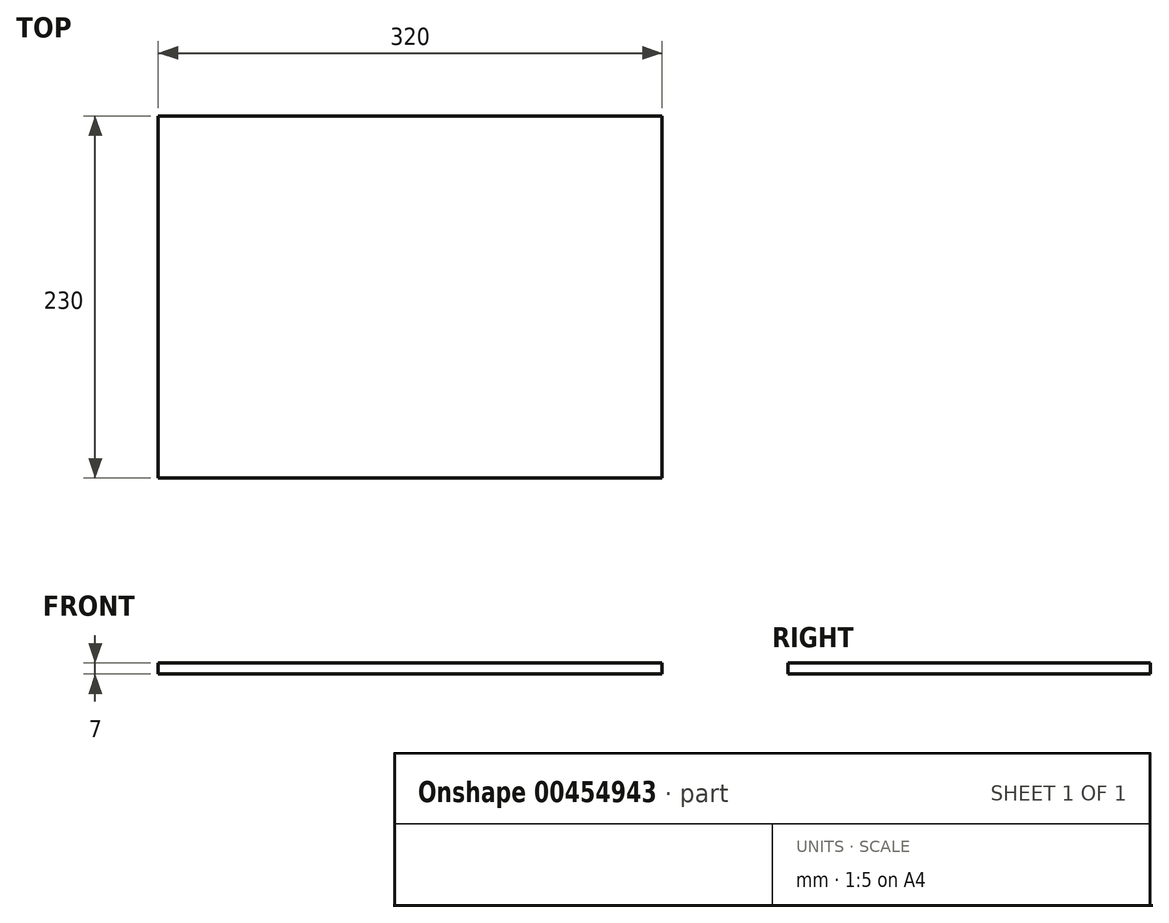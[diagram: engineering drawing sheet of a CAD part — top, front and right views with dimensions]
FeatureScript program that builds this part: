
annotation { "Feature Type Name" : "Feature", "Feature Type Description" : "" }
export const myFeature = defineFeature(function(context is Context, id is Id, definition is map)
    precondition{}
    {
        {
            var Q0;
            Q0=qCreatedBy(makeId("Top.planeOp"),FACE);
            var sketch = newSketch(context, id + "F0", { "sketchPlane" : qUnion([Q0])});
            skLineSegment(sketch, "E0.bottom", {"start": v(-154.74, 172.25) * mm, "end": v(165.26, 172.25) * mm});
            skLineSegment(sketch, "E0.top", {"start": v(-154.74, -57.75) * mm, "end": v(165.26, -57.75) * mm});
            skLineSegment(sketch, "E0.left", {"start": v(-154.74, 172.25) * mm, "end": v(-154.74, -57.75) * mm});
            skLineSegment(sketch, "E0.right", {"start": v(165.26, 172.25) * mm, "end": v(165.26, -57.75) * mm});
            skSolve(sketch);
        }
        {
            var Q0;
            Q0=makeQuery(id+"F0.imprint","IMPRINT",FACE,{"disambiguationData":[TD([[makeQuery(id+"F0.imprint","IMPRINT",EDGE,{"derivedFrom":sQuery(id+"F0.wireOp",EDGE,"E0.bottom")}),-1.0]])]});
            extrude(context, id + "F1", {"entities" : qUnion([Q0]), "depth" : 7 * mm});
        }
    });
